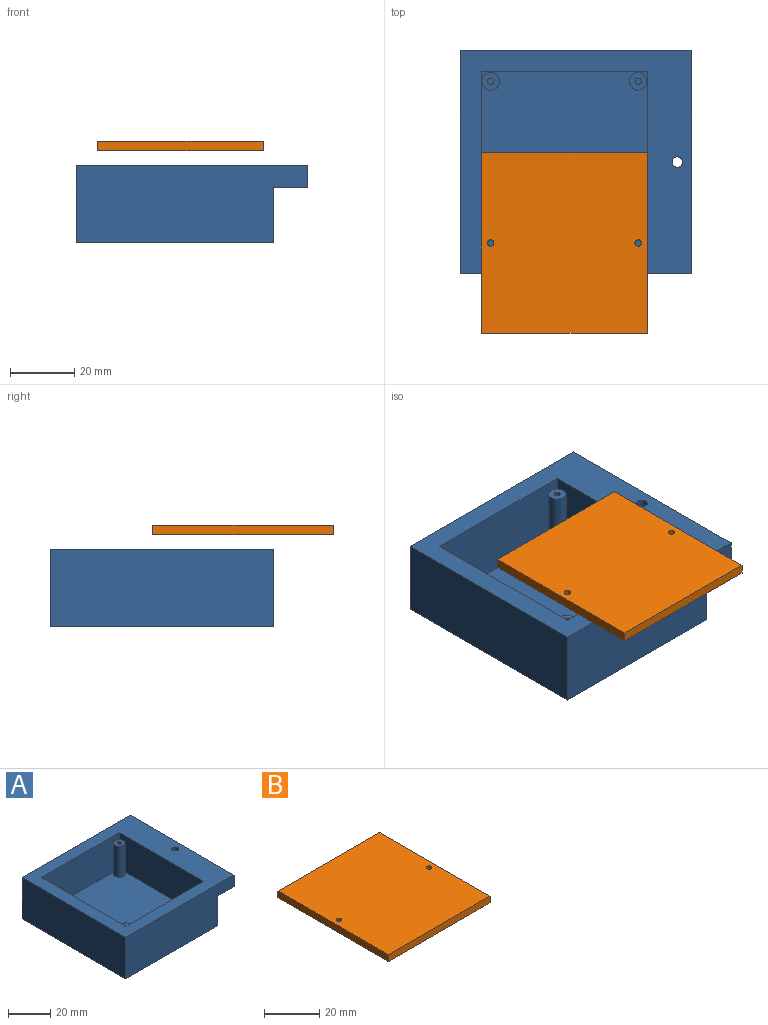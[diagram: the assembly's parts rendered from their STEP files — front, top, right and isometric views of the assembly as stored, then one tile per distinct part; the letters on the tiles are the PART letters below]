
ASSEMBLY  parts=2 mates=1
PART A: 32 faces, bbox 72.2x69.5x24 mm
  f0: cylinder r=1.62mm len=4.8mm, axis (0,0,1), area 49mm2, adj f2,f14
  f1: plane 56.5x21mm, normal (-1,0,0), area 1186.5mm2, adj f2,f8,f9,f11
  f2: plane 72.2x69.5mm, normal (0,0,1), area 2071.6mm2, adj f0,f1,f3,f4,f6,f9,f10,f11
  f3: plane 69.5x24mm, normal (-1,0,0), area 1668mm2, adj f2,f4,f6,f7
  f4: plane 72.2x24mm, normal (0,-1,0), area 1548.8mm2, adj f2,f3,f5,f7,f12,f13
  f5: plane 69.5x17.2mm, normal (1,0,0), area 1195.4mm2, adj f4,f6,f7,f12
  f6: plane 72.2x24mm, normal (0,1,0), area 1548.8mm2, adj f2,f3,f5,f7,f12,f13
  f7: plane 69.5x61.5mm, normal (0,0,-1), area 4274.2mm2, adj f3,f4,f5,f6
  f8: plane 56.5x52mm, normal (0,0,1), area 2843mm2, adj f1,f9,f10,f11,f17,f21,f25,f29
  f9: plane 52x21mm, normal (0,-1,0), area 1092mm2, adj f1,f2,f8,f10
  f10: plane 56.5x21mm, normal (1,0,0), area 1186.5mm2, adj f2,f8,f9,f11
  f11: plane 52x21mm, normal (0,1,0), area 1092mm2, adj f1,f2,f8,f10
  f12: plane 69.5x10.7mm, normal (0,0,-1), area 720.7mm2, adj f4,f5,f6,f13,f15
  f13: plane 69.5x6.8mm, normal (1,0,0), area 472.6mm2, adj f2,f4,f6,f12
  f14: plane 5.4x5.4mm, normal (0,0,-1), area 14.6mm2, adj f0,f15
  f15: cylinder r=2.7mm len=5.4mm, axis (0,0,-1), area 33.9mm2, adj f12,f14
  f16: cylinder r=1mm len=10mm, axis (0,0,-1), area 62.8mm2, adj f18,f19
  f17: cylinder r=2.75mm len=10mm, axis (0,0,-1), area 172.8mm2, adj f8,f18
  f18: plane 5.5x5.5mm, normal (0,0,1), area 20.6mm2, adj f16,f17
  f19: plane 2x2mm, normal (0,0,1), area 3.1mm2, adj f16
  f20: cylinder r=1mm len=10mm, axis (0,0,-1), area 62.8mm2, adj f22,f23
  f21: cylinder r=2.75mm len=10mm, axis (0,0,-1), area 172.8mm2, adj f8,f22
  f22: plane 5.5x5.5mm, normal (0,0,1), area 20.6mm2, adj f20,f21
  f23: plane 2x2mm, normal (0,0,1), area 3.1mm2, adj f20
  f24: cylinder r=1mm len=18mm, axis (0,0,-1), area 113.1mm2, adj f26,f27
  f25: cylinder r=2.75mm len=18mm, axis (0,0,-1), area 311mm2, adj f8,f26
  f26: plane 5.5x5.5mm, normal (0,0,1), area 20.6mm2, adj f24,f25
  f27: plane 2x2mm, normal (0,0,1), area 3.1mm2, adj f24
  f28: cylinder r=1mm len=18mm, axis (0,0,-1), area 113.1mm2, adj f30,f31
  f29: cylinder r=2.75mm len=18mm, axis (0,0,-1), area 311mm2, adj f8,f30
  f30: plane 5.5x5.5mm, normal (0,0,1), area 20.6mm2, adj f28,f29
  f31: plane 2x2mm, normal (0,0,1), area 3.1mm2, adj f28
PART B: 8 faces, bbox 51.8x56.3x3 mm
  f0: plane 56.3x3mm, normal (-1,0,0), area 168.9mm2, adj f1,f3,f4,f5
  f1: plane 51.8x3mm, normal (0,-1,0), area 155.4mm2, adj f0,f2,f4,f5
  f2: plane 56.3x3mm, normal (1,0,0), area 168.9mm2, adj f1,f3,f4,f5
  f3: plane 51.8x3mm, normal (0,1,0), area 155.4mm2, adj f0,f2,f4,f5
  f4: plane 56.3x51.8mm, normal (0,0,1), area 2910.1mm2, adj f0,f1,f2,f3,f6,f7
  f5: plane 56.3x51.8mm, normal (0,0,-1), area 2910.1mm2, adj f0,f1,f2,f3,f6,f7
  f6: cylinder r=1mm len=3mm, axis (0,0,1), area 18.8mm2, adj f4,f5
  f7: cylinder r=1mm len=3mm, axis (0,0,1), area 18.8mm2, adj f4,f5
PLACE A t=(-44.59,-4.63,1.8)mm
PLACE B t=(-37.99,-23.28,30.44)mm
MATE cylindrical B.f7 <-> A.f24  axis (0,0,1) through (-35.09,4.87,33.44)mm
